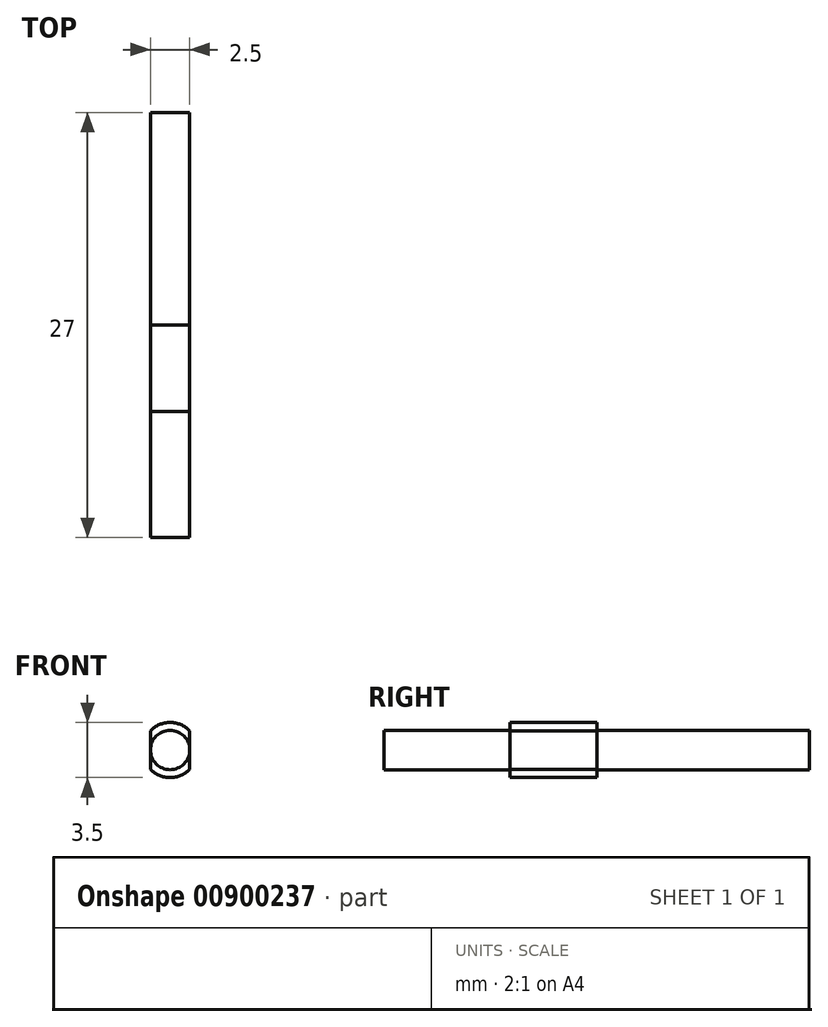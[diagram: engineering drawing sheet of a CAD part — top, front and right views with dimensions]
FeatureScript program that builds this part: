
annotation { "Feature Type Name" : "Feature", "Feature Type Description" : "" }
export const myFeature = defineFeature(function(context is Context, id is Id, definition is map)
    precondition{}
    {
        {
            var Q0;
            Q0=qCreatedBy(makeId("Front.planeOp"),FACE);
            var sketch = newSketch(context, id + "F0", { "sketchPlane" : qUnion([Q0])});
            skArc(sketch, "E0", {"start": v(-1.25, -1.22) * mm, "mid": v(0, -1.75) * mm, "end": v(1.25, -1.22) * mm});
            skLineSegment(sketch, "E1", {"start": v(-1.25, 1.22) * mm, "end": v(-1.25, -1.22) * mm});
            skLineSegment(sketch, "E2", {"start": v(1.25, 1.22) * mm, "end": v(1.25, -1.22) * mm});
            skArc(sketch, "E3.trimOffspring", {"start": v(1.25, 1.22) * mm, "mid": v(0, 1.75) * mm, "end": v(-1.25, 1.22) * mm});
            skSolve(sketch);
        }
        {
            var Q0;
            Q0 = qSketchRegion(id + "F0", true);
            extrude(context, id + "F1", {"entities" : qUnion([Q0]), "depth" : 5.5 * mm, "offsetDistance" : 25 * mm});
        }
        {
            var Q0;
            Q0=qCreatedBy(makeId("Front.planeOp"),FACE);
            var sketch = newSketch(context, id + "F2", { "sketchPlane" : qUnion([Q0])});
            skCircle(sketch, "E4", {"center": v(0, 0) * mm, "radius": 1.25 * mm});
            skSolve(sketch);
        }
        {
            var Q0;
            Q0 = qSketchRegion(id + "F2", true);
            extrude(context, id + "F3", {"entities" : qUnion([Q0]), "operationType" : NewBodyOperationType.ADD, "depth" : 27 * mm, "offsetDistance" : 25 * mm, "symmetric" : true});
        }
    });
